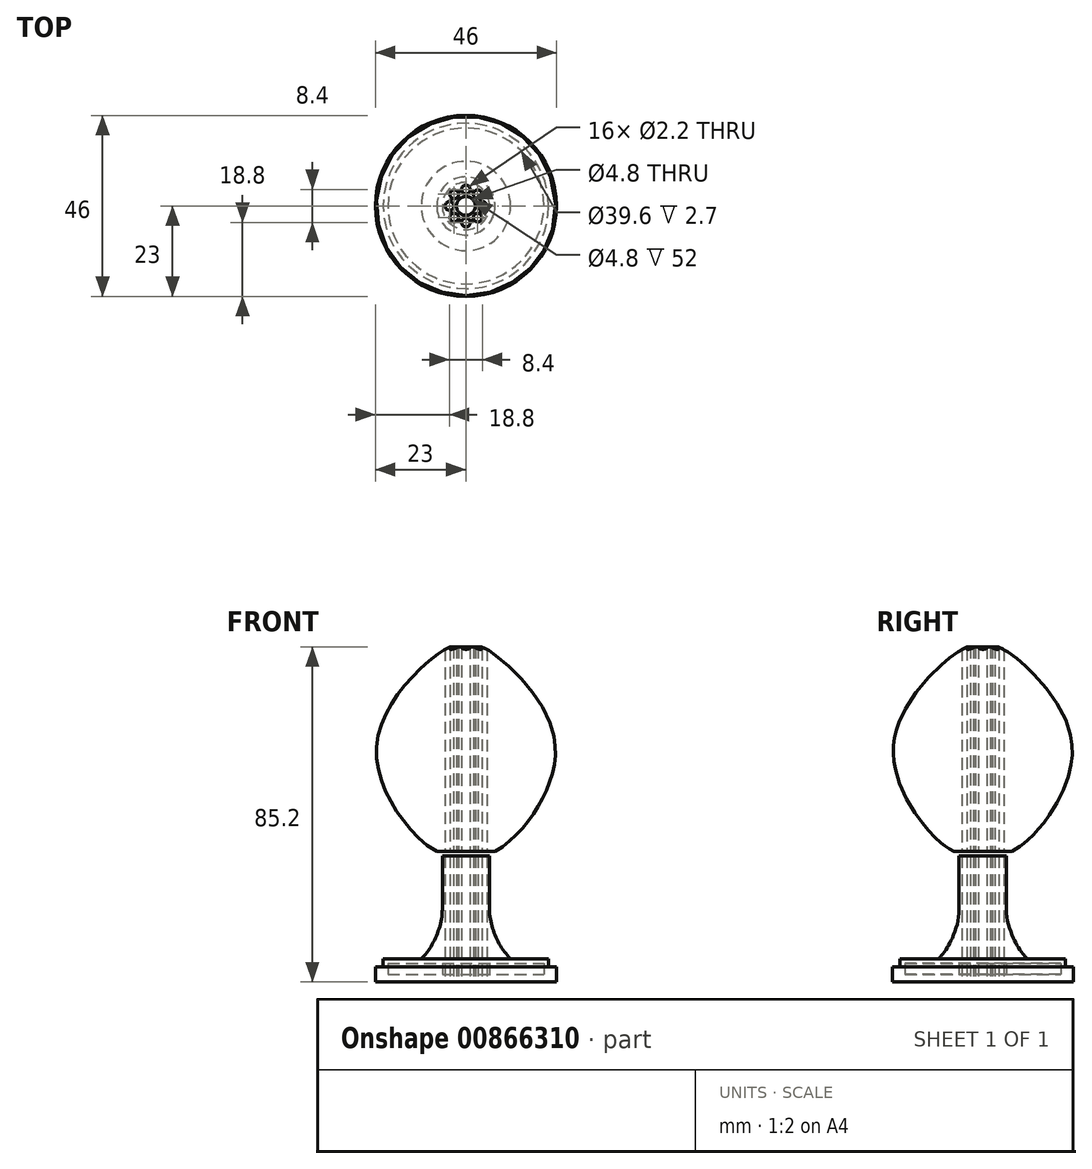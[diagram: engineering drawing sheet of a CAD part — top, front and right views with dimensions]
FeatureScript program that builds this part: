
annotation { "Feature Type Name" : "Feature", "Feature Type Description" : "" }
export const myFeature = defineFeature(function(context is Context, id is Id, definition is map)
    precondition{}
    {
        {
            var Q0;
            Q0=qCreatedBy(makeId("Front.planeOp"),FACE);
            var sketch = newSketch(context, id + "F0", { "sketchPlane" : qUnion([Q0])});
            skLineSegment(sketch, "E0", {"start": v(0, 0) * mm, "end": v(2.4, 0) * mm, "construction": true});
            skLineSegment(sketch, "E1", {"start": v(23, 0) * mm, "end": v(23, 3.9) * mm});
            skLineSegment(sketch, "E2", {"start": v(23, 3.9) * mm, "end": v(21, 3.9) * mm});
            skLineSegment(sketch, "E3", {"start": v(21, 3.9) * mm, "end": v(21, 5.9) * mm});
            skLineSegment(sketch, "E4", {"start": v(21, 5.9) * mm, "end": v(8, 5.9) * mm});
            skLineSegment(sketch, "E5", {"start": v(8, 5.9) * mm, "end": v(8, 7) * mm});
            skLineSegment(sketch, "E6", {"start": v(8, 7) * mm, "end": v(6, 7) * mm});
            skArc(sketch, "E7", {"start": v(6, 30) * mm, "mid": v(6.24, 31) * mm, "end": v(6, 32) * mm});
            skLineSegment(sketch, "E8", {"start": v(2.4, 32) * mm, "end": v(2.4, 0) * mm});
            skLineSegment(sketch, "E9", {"start": v(2.4, 0) * mm, "end": v(23, 0) * mm});
            skLineSegment(sketch, "E10", {"start": v(2.4, 32) * mm, "end": v(6, 32) * mm});
            skLineSegment(sketch, "E11", {"start": v(0, 0) * mm, "end": v(0, 62.1) * mm, "construction": true});
            skLineSegment(sketch, "E12", {"start": v(6, 32) * mm, "end": v(6, 30) * mm, "construction": true});
            skLineSegment(sketch, "E13", {"start": v(4, 31) * mm, "end": v(6, 31) * mm, "construction": true});
            skLineSegment(sketch, "E14", {"start": v(6, 30) * mm, "end": v(6, 7) * mm, "construction": true});
            skLineSegment(sketch, "E15", {"start": v(6, 26.1) * mm, "end": v(6, 9.34) * mm});
            skLineSegment(sketch, "E16.bottom", {"start": v(6, 4.7) * mm, "end": v(19.8, 4.7) * mm});
            skLineSegment(sketch, "E16.top", {"start": v(6, 2) * mm, "end": v(19.8, 2) * mm});
            skLineSegment(sketch, "E16.left", {"start": v(6, 4.7) * mm, "end": v(6, 2) * mm});
            skLineSegment(sketch, "E16.right", {"start": v(19.8, 4.7) * mm, "end": v(19.8, 2) * mm});
            skLineSegment(sketch, "E17", {"start": v(6, 4.7) * mm, "end": v(12.9, 4.7) * mm});
            skLineSegment(sketch, "E18", {"start": v(6, 32) * mm, "end": v(6, 26.1) * mm});
            skFitSpline(sketch, "E19", {"points": [v(12.9, 32) * mm, v(6, 18.5) * mm, v(12.9, 4.7) * mm, v(19.8, 4.7) * mm], "startDerivative": vector(-27.7, -33.14) * mm, "endDerivative": vector(27.4, 7.98) * mm});
            skFitSpline(sketch, "E20", {"points": [v(12.9, 32) * mm, v(9.54, 30.5) * mm, v(6, 32) * mm], "startDerivative": vector(-6.74, -4.55) * mm, "endDerivative": vector(-7.06, 4.51) * mm});
            skSolve(sketch);
        }
        {
            var Q0;
            Q0=qCreatedBy(makeId("Front.planeOp"),FACE);
            var sketch = newSketch(context, id + "F1", { "sketchPlane" : qUnion([Q0])});
            skFitSpline(sketch, "E21", {"points": [v(6, 32) * mm, v(23.23, 36.13) * mm, v(50.32, 52.4) * mm, v(63.37, 54.51) * mm], "startDerivative": vector(14.56, 0) * mm, "endDerivative": vector(27.15, -10.06) * mm});
            skLineSegment(sketch, "E22", {"start": v(63.37, 54.51) * mm, "end": v(64, 55) * mm});
            skLineSegment(sketch, "E23", {"start": v(2.4, 33.2) * mm, "end": v(2.4, 32) * mm});
            skLineSegment(sketch, "E24.0", {"start": v(2.4, 32) * mm, "end": v(6, 32) * mm});
            skFitSpline(sketch, "E25.0", {"points": [v(6, 33.2) * mm, v(6.05, 33.2) * mm, v(6.2, 33.2) * mm, v(6.66, 33.23) * mm, v(7.47, 33.3) * mm, v(8.76, 33.46) * mm, v(10.84, 33.78) * mm, v(14, 34.4) * mm, v(17.6, 35.35) * mm, v(20.55, 36.34) * mm, v(22.76, 37.2) * mm, v(24.93, 38.2) * mm, v(27.78, 39.68) * mm, v(31.28, 41.77) * mm, v(35.37, 44.5) * mm, v(39.37, 47.26) * mm, v(42.64, 49.46) * mm, v(45.24, 51.08) * mm, v(47.18, 52.2) * mm, v(49.12, 53.2) * mm, v(51.06, 54.05) * mm, v(52.98, 54.76) * mm, v(55.46, 55.5) * mm, v(58.38, 56.06) * mm, v(60.91, 56.17) * mm, v(62.65, 55.97) * mm, v(63.42, 55.77) * mm, v(63.78, 55.64) * mm]});
            skLineSegment(sketch, "E26", {"start": v(2.4, 33.2) * mm, "end": v(6, 33.2) * mm});
            skArc(sketch, "E27", {"start": v(63.37, 55.77) * mm, "mid": v(63.8, 55.48) * mm, "end": v(64, 55) * mm});
            skSolve(sketch);
        }
        {
            var Q0;
            Q0=qCreatedBy(makeId("Front.planeOp"),FACE);
            var sketch = newSketch(context, id + "F2", { "sketchPlane" : qUnion([Q0])});
            skLineSegment(sketch, "E28.0", {"start": v(7.4, 33.2) * mm, "end": v(2.4, 33.2) * mm});
            skLineSegment(sketch, "E29", {"start": v(2.4, 33.2) * mm, "end": v(2.4, 85.2) * mm});
            skLineSegment(sketch, "E30", {"start": v(2.4, 85.2) * mm, "end": v(4, 85.2) * mm});
            skPoint(sketch, "E31.0", {"position": v(2.4, 33.2) * mm});
            skLineSegment(sketch, "E32", {"start": v(3.6, 73.19) * mm, "end": v(3.6, 34.32) * mm});
            skLineSegment(sketch, "E33", {"start": v(3.6, 34.32) * mm, "end": v(6.26, 34.32) * mm});
            skPoint(sketch, "E34.visualSharp", {"position": v(3.6, 77.45) * mm});
            skArc(sketch, "E34.filletArc", {"start": v(4.2, 73.23) * mm, "mid": v(3.88, 73.49) * mm, "end": v(3.6, 73.19) * mm});
            skFitSpline(sketch, "E35", {"points": [v(2.4, 33.2) * mm, v(7.4, 33.2) * mm, v(22.62, 60.84) * mm, v(4, 85.2) * mm, v(2.4, 85.2) * mm], "startDerivative": vector(27.18, -10.59) * mm, "endDerivative": vector(-12.71, -5.79) * mm});
            skSolve(sketch);
        }
        {
            var Q0;
            Q0=qCreatedBy(makeId("Front.planeOp"),FACE);
            var sketch = newSketch(context, id + "F3", { "sketchPlane" : qUnion([Q0])});
            skLineSegment(sketch, "E36.0", {"start": v(2.4, 85.2) * mm, "end": v(4, 85.2) * mm});
            skFitSpline(sketch, "E37", {"points": [v(4, 85.2) * mm, v(18.4, 91.4) * mm, v(24.76, 95.66) * mm, v(30.68, 98.29) * mm, v(34.8, 97.2) * mm], "startDerivative": vector(68.77, 13.98) * mm, "endDerivative": vector(7.22, -12.54) * mm});
            skFitSpline(sketch, "E38.0", {"points": [v(3.76, 86.38) * mm, v(6.57, 86.95) * mm, v(9.85, 87.94) * mm, v(13.04, 89.4) * mm, v(15, 90.53) * mm, v(16.45, 91.5) * mm, v(17.57, 92.27) * mm, v(18.7, 93.05) * mm, v(20.07, 94) * mm, v(21.7, 95.09) * mm, v(23.05, 95.98) * mm, v(24.11, 96.67) * mm, v(25.18, 97.37) * mm, v(26.57, 98.21) * mm, v(28.06, 98.9) * mm, v(29.36, 99.3) * mm, v(30.2, 99.45) * mm, v(30.91, 99.51) * mm, v(31.62, 99.53) * mm, v(32.48, 99.47) * mm, v(33.47, 99.3) * mm, v(34.22, 99.05) * mm, v(34.77, 98.79) * mm, v(35.16, 98.55) * mm, v(35.53, 98.24) * mm, v(35.75, 97.96) * mm, v(35.84, 97.8) * mm]});
            skLineSegment(sketch, "E39", {"start": v(4, 86.43) * mm, "end": v(4, 120.2) * mm});
            skLineSegment(sketch, "E40", {"start": v(2, 140.2) * mm, "end": v(2.4, 85.2) * mm});
            skLineSegment(sketch, "E41", {"start": v(34.8, 97.2) * mm, "end": v(35.84, 97.8) * mm});
            skLineSegment(sketch, "E42", {"start": v(4, 120.2) * mm, "end": v(4, 139.8) * mm, "construction": true});
            skPoint(sketch, "E43.visualSharp", {"position": v(10.68, 119.56) * mm});
            skLineSegment(sketch, "E44", {"start": v(4, 138.13) * mm, "end": v(4, 121.8) * mm});
            skFitSpline(sketch, "E45", {"points": [v(4, 120.2) * mm, v(20.08, 124.48) * mm, v(31.86, 143.47) * mm, v(29.84, 145.15) * mm, v(28.08, 141.45) * mm, v(17.7, 127.56) * mm, v(6.36, 157.2) * mm, v(2, 140.2) * mm], "startDerivative": vector(103.88, 0.96) * mm, "endDerivative": vector(-23.7, -182.02) * mm});
            skSolve(sketch);
        }
        {
            var Q0;
            Q0=makeQuery(id+"F2.imprint","IMPRINT",FACE,{"disambiguationData":[TD([[makeQuery(id+"F2.imprint","IMPRINT",EDGE,{"derivedFrom":sQuery(id+"F2.wireOp",EDGE,"E28.0")}),-1.0]])]});
            var Q1;
            Q1=makeQuery(id+"F1.imprint","IMPRINT",FACE,{"disambiguationData":[TD([[makeQuery(id+"F1.imprint","IMPRINT",EDGE,{"derivedFrom":sQuery(id+"F1.wireOp",EDGE,"E21")}),1.0]])]});
            var Q2;
            Q2=makeQuery(id+"F0.imprint","IMPRINT",FACE,{"disambiguationData":[TD([[makeQuery(id+"F0.imprint","IMPRINT",EDGE,{"derivedFrom":sQuery(id+"F0.wireOp",EDGE,"E1")}),1.0]])]});
            var Q3;
            Q3=makeQuery(id+"F3.imprint","IMPRINT",FACE,{"disambiguationData":[TD([[makeQuery(id+"F3.imprint","IMPRINT",EDGE,{"derivedFrom":sQuery(id+"F3.wireOp",EDGE,"E36.0")}),1.0]])]});
            var Q4;
            Q4=sQuery(id+"F0.wireOp",EDGE,"E11");
            revolve(context, id + "F4", {"entities" : qUnion([Q0, Q1, Q2, Q3]), "axis" : qUnion([Q4]), "revolveType" : RevolveType.FULL});
        }
        {
            var Q0;
            Q0=makeQuery(id+"F4.opRevolve","SWEPT_FACE",FACE,{"disambiguationData":[OSD([sQuery(id+"F0.wireOp",EDGE,"E9")])]});
            var sketch = newSketch(context, id + "F5", { "sketchPlane" : qUnion([Q0])});
            skCircle(sketch, "E46", {"center": v(4.2, 0) * mm, "radius": 1.1 * mm});
            skCircle(sketch, "E47.0", {"center": v(0, 0) * mm, "radius": 6 * mm, "construction": true});
            skCircle(sketch, "E48.1.0", {"center": v(2.97, 2.97) * mm, "radius": 1.1 * mm});
            skCircle(sketch, "E48.2.0", {"center": v(0, 4.2) * mm, "radius": 1.1 * mm});
            skCircle(sketch, "E48.3.0", {"center": v(-2.97, 2.97) * mm, "radius": 1.1 * mm});
            skCircle(sketch, "E48.4.0", {"center": v(-4.2, 0) * mm, "radius": 1.1 * mm});
            skCircle(sketch, "E48.5.0", {"center": v(-2.97, -2.97) * mm, "radius": 1.1 * mm});
            skCircle(sketch, "E49.1.6.0", {"center": v(0, -4.2) * mm, "radius": 1.1 * mm});
            skCircle(sketch, "E49.1.7.0", {"center": v(2.97, -2.97) * mm, "radius": 1.1 * mm});
            skSolve(sketch);
        }
        {
            var Q0;
            Q0=qSketchRegion(id+"F5",true);
            extrude(context, id + "F6", {"entities" : qUnion([Q0]), "operationType" : NewBodyOperationType.REMOVE, "endBound" : BoundingType.THROUGH_ALL, "oppositeDirection" : true, "depth" : 25 * mm});
        }
    });
